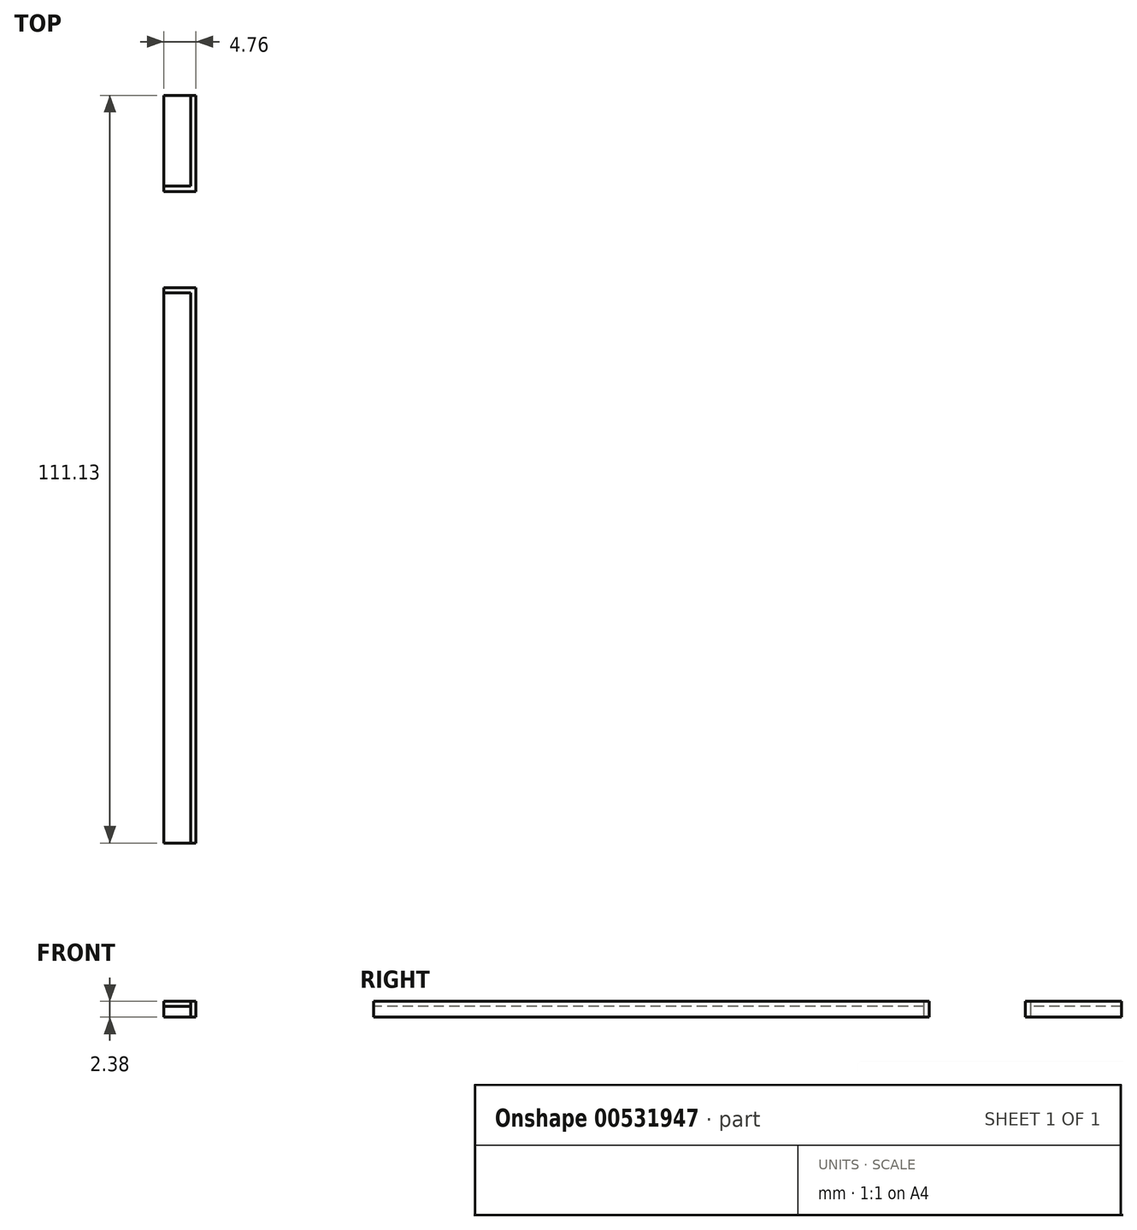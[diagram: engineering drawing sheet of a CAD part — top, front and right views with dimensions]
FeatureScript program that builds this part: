
annotation { "Feature Type Name" : "Feature", "Feature Type Description" : "" }
export const myFeature = defineFeature(function(context is Context, id is Id, definition is map)
    precondition{}
    {
        {
            var Q0;
            Q0=qCreatedBy(makeId("Top.planeOp"),FACE);
            var sketch = newSketch(context, id + "F0", { "sketchPlane" : qUnion([Q0])});
            skLineSegment(sketch, "E0.bottom", {"start": v(-16.06, 56.63) * mm, "end": v(-11.3, 56.63) * mm});
            skLineSegment(sketch, "E0.top", {"start": v(-16.06, -54.5) * mm, "end": v(-11.3, -54.5) * mm});
            skLineSegment(sketch, "E0.left", {"start": v(-16.06, 56.63) * mm, "end": v(-16.06, -54.5) * mm});
            skLineSegment(sketch, "E0.right", {"start": v(-11.3, 56.63) * mm, "end": v(-11.3, -54.5) * mm});
            skLineSegment(sketch, "E1", {"start": v(-16.06, 42.34) * mm, "end": v(-11.3, 42.34) * mm});
            skLineSegment(sketch, "E2", {"start": v(-16.06, 28.05) * mm, "end": v(-11.3, 28.05) * mm});
            skLineSegment(sketch, "E3", {"start": v(-12.09, 56.63) * mm, "end": v(-12.09, 42.34) * mm});
            skLineSegment(sketch, "E4", {"start": v(-11.3, 43.14) * mm, "end": v(-16.06, 43.14) * mm});
            skLineSegment(sketch, "E5", {"start": v(-16.06, 27.26) * mm, "end": v(-11.3, 27.26) * mm});
            skLineSegment(sketch, "E6", {"start": v(-12.09, 28.05) * mm, "end": v(-12.09, -54.5) * mm});
            skSolve(sketch);
        }
        {
            var Q0;
            {var subQ0=sQuery(id+"F0.wireOp",EDGE,"E0.right");var subQ1=sQuery(id+"F0.wireOp",EDGE,"E0.bottom");var subQ2=makeQuery(id+"F0.imprint","INTERSECT",VERTEX,{"derivedFrom":[subQ1,subQ0]});Q0=makeQuery(id+"F0.imprint","IMPRINT",FACE,{"disambiguationData":[TD([[makeQuery(id+"F0.imprint","IMPRINT",EDGE,{"disambiguationData":[TD([[subQ2,1.0]])],"derivedFrom":subQ1}),-1.0]])]});}
            var Q1;
            {var subQ0=sQuery(id+"F0.wireOp",EDGE,"E0.right");var subQ1=sQuery(id+"F0.wireOp",EDGE,"E0.top");var subQ2=makeQuery(id+"F0.imprint","INTERSECT",VERTEX,{"derivedFrom":[subQ1,subQ0]});Q1=makeQuery(id+"F0.imprint","IMPRINT",FACE,{"disambiguationData":[TD([[makeQuery(id+"F0.imprint","IMPRINT",EDGE,{"disambiguationData":[TD([[subQ2,1.0]])],"derivedFrom":subQ1}),1.0]])]});}
            var Q2;
            {var subQ0=sQuery(id+"F0.wireOp",EDGE,"E1");var subQ1=sQuery(id+"F0.wireOp",EDGE,"E0.left");var subQ2=makeQuery(id+"F0.imprint","INTERSECT",VERTEX,{"derivedFrom":[subQ1,subQ0]});Q2=makeQuery(id+"F0.imprint","IMPRINT",FACE,{"disambiguationData":[TD([[makeQuery(id+"F0.imprint","IMPRINT",EDGE,{"disambiguationData":[TD([[subQ2,1.0]])],"derivedFrom":subQ1}),1.0]])]});}
            var Q3;
            {var subQ0=sQuery(id+"F0.wireOp",EDGE,"E2");var subQ1=sQuery(id+"F0.wireOp",EDGE,"E0.left");var subQ2=makeQuery(id+"F0.imprint","INTERSECT",VERTEX,{"derivedFrom":[subQ1,subQ0]});Q3=makeQuery(id+"F0.imprint","IMPRINT",FACE,{"disambiguationData":[TD([[makeQuery(id+"F0.imprint","IMPRINT",EDGE,{"disambiguationData":[TD([[subQ2,-1.0]])],"derivedFrom":subQ1}),1.0]])]});}
            var Q4;
            {var subQ0=sQuery(id+"F0.wireOp",EDGE,"E1");var subQ1=sQuery(id+"F0.wireOp",EDGE,"E0.right");var subQ2=makeQuery(id+"F0.imprint","INTERSECT",VERTEX,{"derivedFrom":[subQ1,subQ0]});Q4=makeQuery(id+"F0.imprint","IMPRINT",FACE,{"disambiguationData":[TD([[makeQuery(id+"F0.imprint","IMPRINT",EDGE,{"disambiguationData":[TD([[subQ2,1.0]])],"derivedFrom":subQ1}),-1.0]])]});}
            var Q5;
            {var subQ0=sQuery(id+"F0.wireOp",EDGE,"E2");var subQ1=sQuery(id+"F0.wireOp",EDGE,"E0.right");var subQ2=makeQuery(id+"F0.imprint","INTERSECT",VERTEX,{"derivedFrom":[subQ1,subQ0]});Q5=makeQuery(id+"F0.imprint","IMPRINT",FACE,{"disambiguationData":[TD([[makeQuery(id+"F0.imprint","IMPRINT",EDGE,{"disambiguationData":[TD([[subQ2,-1.0]])],"derivedFrom":subQ1}),-1.0]])]});}
            extrude(context, id + "F1", {"entities" : qUnion([Q0, Q1, Q2, Q3, Q4, Q5]), "depth" : 2.38 * mm, "offsetDistance" : 25.4 * mm});
        }
        {
            var Q0;
            {var subQ0=sQuery(id+"F0.wireOp",EDGE,"E0.left");var subQ1=sQuery(id+"F0.wireOp",EDGE,"E0.bottom");var subQ2=makeQuery(id+"F0.imprint","INTERSECT",VERTEX,{"derivedFrom":[subQ1,subQ0]});Q0=makeQuery(id+"F0.imprint","IMPRINT",FACE,{"disambiguationData":[TD([[makeQuery(id+"F0.imprint","IMPRINT",EDGE,{"disambiguationData":[TD([[subQ2,-1.0]])],"derivedFrom":subQ1}),-1.0]])]});}
            var Q1;
            {var subQ0=sQuery(id+"F0.wireOp",EDGE,"E0.left");var subQ1=sQuery(id+"F0.wireOp",EDGE,"E0.top");var subQ2=makeQuery(id+"F0.imprint","INTERSECT",VERTEX,{"derivedFrom":[subQ1,subQ0]});Q1=makeQuery(id+"F0.imprint","IMPRINT",FACE,{"disambiguationData":[TD([[makeQuery(id+"F0.imprint","IMPRINT",EDGE,{"disambiguationData":[TD([[subQ2,-1.0]])],"derivedFrom":subQ1}),1.0]])]});}
            extrude(context, id + "F2", {"entities" : qUnion([Q0, Q1]), "depth" : 1.59 * mm, "offsetDistance" : 25.4 * mm});
        }
    });
